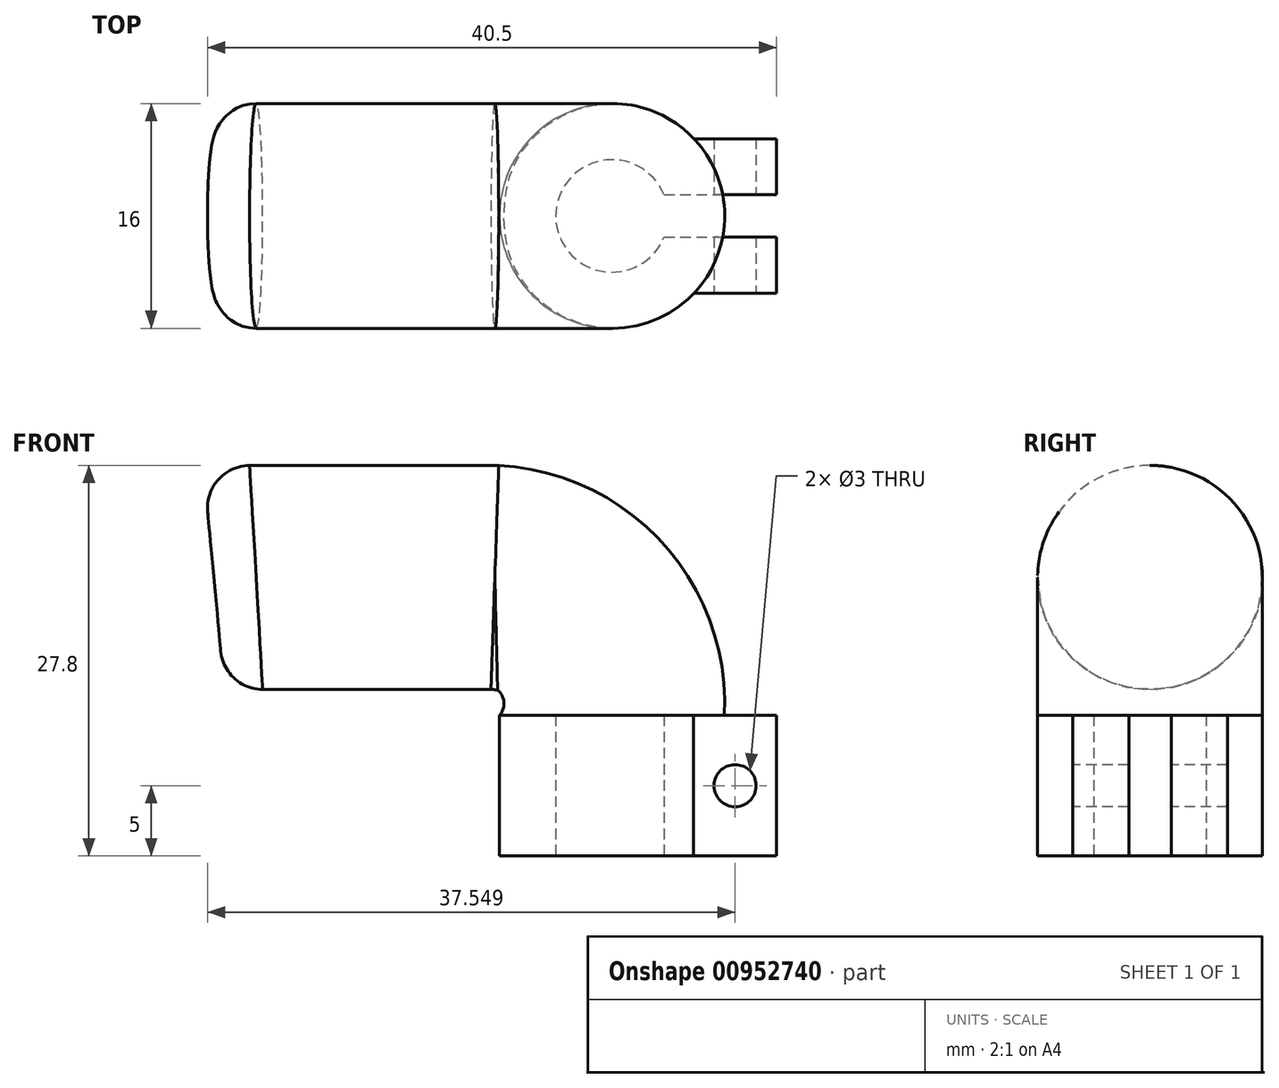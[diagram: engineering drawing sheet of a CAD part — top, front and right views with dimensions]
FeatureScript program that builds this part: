
annotation { "Feature Type Name" : "Feature", "Feature Type Description" : "" }
export const myFeature = defineFeature(function(context is Context, id is Id, definition is map)
    precondition{}
    {
        {
            var Q0;
            Q0=qCreatedBy(makeId("Top.planeOp"),FACE);
            var sketch = newSketch(context, id + "F0", { "sketchPlane" : qUnion([Q0])});
            skArc(sketch, "E0", {"start": v(3.7, 1.5) * mm, "mid": v(-4, 0) * mm, "end": v(3.7, -1.5) * mm});
            skLineSegment(sketch, "E1", {"start": v(3.7, 1.5) * mm, "end": v(11.7, 1.5) * mm});
            skLineSegment(sketch, "E2.MirrorCS", {"start": v(3.7, -1.5) * mm, "end": v(11.7, -1.5) * mm});
            skLineSegment(sketch, "E3.0", {"start": v(5.8, -5.5) * mm, "end": v(11.7, -5.5) * mm});
            skArc(sketch, "E3.1", {"start": v(5.8, 5.5) * mm, "mid": v(-8, 0) * mm, "end": v(5.8, -5.5) * mm});
            skLineSegment(sketch, "E3.2", {"start": v(5.8, 5.5) * mm, "end": v(11.7, 5.5) * mm});
            skLineSegment(sketch, "E4", {"start": v(11.7, 5.5) * mm, "end": v(11.7, 1.5) * mm});
            skLineSegment(sketch, "E5", {"start": v(11.7, -1.5) * mm, "end": v(11.7, -5.5) * mm});
            skSolve(sketch);
        }
        {
            var Q0;
            Q0=makeQuery(id+"F0.imprint","IMPRINT",FACE,{"disambiguationData":[TD([[makeQuery(id+"F0.imprint","IMPRINT",EDGE,{"derivedFrom":sQuery(id+"F0.wireOp",EDGE,"E0")}),-1.0]])]});
            extrude(context, id + "F1", {"entities" : qUnion([Q0]), "depth" : 10 * mm, "offsetDistance" : 25 * mm});
        }
        {
            var Q0;
            Q0=makeQuery(id+"F1.opExtrude","SWEPT_FACE",FACE,{"disambiguationData":[OSD([sQuery(id+"F0.wireOp",EDGE,"E3.0")])]});
            var sketch = newSketch(context, id + "F2", { "sketchPlane" : qUnion([Q0])});
            skCircle(sketch, "E6", {"center": v(8.76, 5) * mm, "radius": 1.5 * mm});
            skPoint(sketch, "E6.centerSnap0", {"position": v(11.7, 5) * mm});
            skLineSegment(sketch, "E7", {"start": v(5.8, 10) * mm, "end": v(11.7, 10) * mm});
            skSolve(sketch);
        }
        {
            var Q0;
            Q0=makeQuery(id+"F2.imprint","IMPRINT",FACE,{"disambiguationData":[TD([[makeQuery(id+"F2.imprint","IMPRINT",EDGE,{"derivedFrom":sQuery(id+"F2.wireOp",EDGE,"E6")}),1.0]])]});
            extrude(context, id + "F3", {"entities" : qUnion([Q0]), "operationType" : NewBodyOperationType.REMOVE, "oppositeDirection" : true, "depth" : 25 * mm, "offsetDistance" : 25 * mm});
        }
        {
            var Q0;
            Q0=makeQuery(id+"F1.opExtrude","CAP_FACE",FACE,{"disambiguationData":[OSD([sQuery(id+"F0.wireOp",EDGE,"E0"),sQuery(id+"F0.wireOp",EDGE,"E1"),sQuery(id+"F0.wireOp",EDGE,"E2.MirrorCS"),sQuery(id+"F0.wireOp",EDGE,"E3.0"),sQuery(id+"F0.wireOp",EDGE,"E3.1"),sQuery(id+"F0.wireOp",EDGE,"E3.2"),sQuery(id+"F0.wireOp",EDGE,"E4"),sQuery(id+"F0.wireOp",EDGE,"E5")])],"isStart":false});
            var sketch = newSketch(context, id + "F4", { "sketchPlane" : qUnion([Q0])});
            skCircle(sketch, "E8", {"center": v(0, 0) * mm, "radius": 8 * mm});
            skSolve(sketch);
        }
        {
            var Q0;
            Q0=qCreatedBy(makeId("Front.planeOp"),FACE);
            var sketch = newSketch(context, id + "F5", { "sketchPlane" : qUnion([Q0])});
            skArc(sketch, "E9", {"start": v(0, 10) * mm, "mid": v(-2.1, 16.67) * mm, "end": v(-8.33, 19.82) * mm});
            skLineSegment(sketch, "E10", {"start": v(-8.33, 19.82) * mm, "end": v(-28.33, 19.82) * mm});
            skPoint(sketch, "E11.orphan", {"position": v(-9.59, 19.82) * mm});
            skSolve(sketch);
        }
        {
            var Q0;
            {var subQ0=makeQuery(id+"F1.opExtrude","CAP_EDGE",EDGE,{"disambiguationData":[OSD([sQuery(id+"F0.wireOp",EDGE,"E0")])],"isStart":false});Q0=makeQuery(id+"F4.imprint","IMPRINT",FACE,{"disambiguationData":[TD([[makeQuery(id+"F4.imprint","IMPRINT",EDGE,{"derivedFrom":subQ0}),-1.0]])]});}
            var Q1;
            {var subQ5=makeQuery(id+"F1.opExtrude","CAP_EDGE",EDGE,{"disambiguationData":[OSD([sQuery(id+"F0.wireOp",EDGE,"E0")])],"isStart":false});Q1=makeQuery(id+"F4.imprint","IMPRINT",FACE,{"disambiguationData":[TD([[makeQuery(id+"F4.imprint","IMPRINT",EDGE,{"derivedFrom":subQ5}),1.0]])]});}
            var Q2;
            Q2=sQuery(id+"F5.wireOp",EDGE,"E9");
            var Q3;
            Q3=sQuery(id+"F5.wireOp",EDGE,"E10");
            sweep(context, id + "F6", {"operationType" : NewBodyOperationType.ADD, "profiles" : qUnion([Q0, Q1]), "path" : qUnion([Q2, Q3])});
        }
        {
            var Q0;
            Q0=makeQuery(id+"F6.opSweep","CAP_EDGE",EDGE,{"disambiguationData":[OSD([sQuery(id+"F4.wireOp",EDGE,"E8"),sQuery(id+"F5.wireOp",VERTEX,"E10.end")])],"isStart":false});
            fillet(context, id + "F7", {"entities" : qUnion([Q0]), "radius" : 3 * mm, "tangentPropagation" : true, "allowEdgeOverflow" : false});
        }
    });
